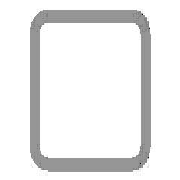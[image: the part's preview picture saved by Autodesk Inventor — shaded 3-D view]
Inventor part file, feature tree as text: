
AUTODESK INVENTOR PART (.ipt)
format: ipt  version: 2022 (Build 260153000, 153)  size: 148,480 bytes
history: native  units: mm (DEFAULTED — no unit token found)
features: other x4, sketch x3, plane x2, extrude x1, split x1
ambient origin geometry x8: Origin, YZ Plane, XZ Plane, XY Plane, X Axis, Y Axis, Z Axis, Center Point
bodies: Solid1 (feature_tree)
feature tree (11):
  parser-record x1  (decoder bookkeeping rows leaked as tree rows — omitted from the tree; the rows remain in map.json)
  other  "Driven Length"
  other  "Plano inicial"
  other  "Plano final"
  extrude  "Cuerpo"  TaperAngle=0.0deg  [1 undecoded]
  plane  "Plano de trabajo4"
  split  "Dividir1"
  sketch  "Boceto"  dims[d10=40.0mm d11=40.0mm d12=5.0mm d13=-11.768067mm d14=300.0mm d15=20.0mm d16=20.0mm d17=90.0deg d18=311.768067mm]
  sketch  "Sketch3"  dims[d3=311.768067mm d4=0.0mm]
  plane  "Work Plane3"
  sketch  "Sketch4"  dims[d7=7.5mm]
note: 1 required parameter value undecoded (feature->parameter linkage not recoverable at this tier; creation-order binding heuristic only, values carry confidence <= 0.55)
